# Revit family: SH-2110
name_source: partatom
category: Lighting Fixtures
revit_build: Autodesk Revit 2017 (Build: 20160225_1515(x64)
units: mm (PartAtom-declared; Revit-internal decimal feet)

## family parameters
Always vertical = No
Cut with Voids When Loaded = No
Light Source = No
OmniClass Number = 23.80.70.00
OmniClass Title = Lighting
Part Type = Normal
Room Calculation Point = No
Round Connector Dimension = Use Diameter
Shared = Yes
Work Plane-Based = Yes

## types (2) — shared parameters
Body Material = Aluminum
Body color = White color
Default Elevation = 121.9 cm
Diffuser = light
Height = 53.7 cm
IP = IP65
Lamp = E40
Manufacturer = SHOA
Model = SH-2110
Protection Class = Class I
Type medule = LAMP
URL = https://www.shoaco.com
Voltage/Frequency = 230V/50HZ
Website = www.shoaco.com
Width = 35.9 cm
consumption current = 5 A
wattage = 400 W

## per-type parameters (varying)
| type | metal halide lampe | sodium lampe |
| Sh-2110(White color-E40-metal halide) | Yes | No |
| Sh-2110(White color-E40-sodium) | No | Yes |

## geometry (parser evidence)
native form markers: Sweep x9
no freeform markers — native parametric forms only
